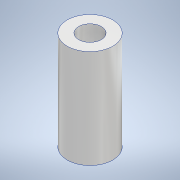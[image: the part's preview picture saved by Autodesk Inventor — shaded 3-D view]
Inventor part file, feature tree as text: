
AUTODESK INVENTOR PART (.ipt)
format: ipt  version: 2020.2 (Build 242310000, 310)  size: 103,936 bytes
history: native  units: mm
features: other x1, extrude x1, sketch x1
ambient origin geometry x8: Origin, YZ Plane, XZ Plane, XY Plane, X Axis, Y Axis, Z Axis, Center Point
bodies: Body1 (feature_tree)
feature tree (3):
  other  "ソリッド1"
  extrude  "押し出し1"  Depth=6.0mm
  sketch  "スケッチ1"
